# Revit family: Power-Fin Boiler PBN2500-5000_2014
name_source: partatom
category: Mechanical Equipment
revit_build: Autodesk Revit 2014 (Build: 20130308_1515(x64)
units: mm (PartAtom-declared; Revit-internal decimal feet)

## types (5) — shared parameters
# of Connections = 1
Control Voltage = 24
Description = Power-Fin Boiler
Drain Radius = 3/8"
Front Clearance Depth = 24"
Manufacturer = Lochinvar
SES BIM Studio # = 2016 0649 05
Top Clearance Depth = 24"
URL = http://www.lochinvar.com
WATER CONN SIZE = 4"
Water Conn Radius = 2"

## per-type parameters (varying)
- PBN2500: AIR INLET SIZE=9"; A_HEIGHT=59"; Air Inlet Radius=4 1/2"; B_LENGTH=44 1/2"; Back Clearance Length=36"; C_WIDTH=29 3/4"; D_Gas Conn Height=49 3/4"; Display Panel Height=6 1/2"; Display Panel width=10 3/4"; E_Gas Conn Offset From Left=4"; F_Vent Offset From Left=15"; GALLON CAPACITY=10.4; GAS CONN SIZE=2"; G_Vent Length=16"; Gas Conn Radius=1"; H_Air Inlet Offset From Top=9"; INPUT RATE (BTUH)=2500000; J_Air Inlet Offset from Left=20 1/4"; K_Water Inlet & Outlet Height=37"; L_Water Outlet Offset From Left=8 3/4"; M_Vent Height=23"; N_Water Inlet Offset From Left=21 1/4"; OUTPUT RATE (BTUH)=2175000; P_Pipe Length=12"; Q_Panel Height=40"; Total Amps=4.9; VENT SIZE=9"; Vent Radius=4 1/2"; Voltage/Heater=240V-1PH
- PBN3000: AIR INLET SIZE=9"; A_HEIGHT=65"; Air Inlet Radius=4 1/2"; B_LENGTH=44 1/2"; Back Clearance Length=36"; C_WIDTH=29 3/4"; D_Gas Conn Height=55 3/4"; Display Panel Height=7"; Display Panel width=10 3/4"; E_Gas Conn Offset From Left=4"; F_Vent Offset From Left=15"; GALLON CAPACITY=11.3; GAS CONN SIZE=2"; G_Vent Length=16 1/4"; Gas Conn Radius=1"; H_Air Inlet Offset From Top=9"; INPUT RATE (BTUH)=3000000; J_Air Inlet Offset from Left=20 1/4"; K_Water Inlet & Outlet Height=43"; L_Water Outlet Offset From Left=8 3/4"; M_Vent Height=23"; N_Water Inlet Offset From Left=21 1/4"; OUTPUT RATE (BTUH)=2610000; P_Pipe Length=12"; Q_Panel Height=45"; Total Amps=4.9; VENT SIZE=10"; Vent Radius=5"; Voltage/Heater=240V-1PH
- PBN3500: AIR INLET SIZE=10"; A_HEIGHT=70 1/4"; Air Inlet Radius=5"; B_LENGTH=47 1/4"; Back Clearance Length=36"; C_WIDTH=29 3/4"; D_Gas Conn Height=62 1/2"; Display Panel Height=6 1/8"; Display Panel width=10 1/2"; E_Gas Conn Offset From Left=8 1/4"; F_Vent Offset From Left=15"; GALLON CAPACITY=12.2; GAS CONN SIZE=2"; G_Vent Length=16 1/4"; Gas Conn Radius=1"; H_Air Inlet Offset From Top=9"; INPUT RATE (BTUH)=3500000; J_Air Inlet Offset from Left=20 1/4"; K_Water Inlet & Outlet Height=48 1/2"; L_Water Outlet Offset From Left=9"; M_Vent Height=23"; N_Water Inlet Offset From Left=21 1/2"; OUTPUT RATE (BTUH)=3045000; P_Pipe Length=12"; Q_Panel Height=52"; Total Amps=6.0; VENT SIZE=10"; Vent Radius=5"; Voltage/Heater=240V-3PH
- PBN4000: AIR INLET SIZE=10"; A_HEIGHT=79 3/4"; Air Inlet Radius=5"; B_LENGTH=47 1/4"; Back Clearance Length=36"; C_WIDTH=29 3/4"; D_Gas Conn Height=68 3/4"; Display Panel Height=7 5/8"; Display Panel width=10 1/2"; E_Gas Conn Offset From Left=8 1/4"; F_Vent Offset From Left=15"; GALLON CAPACITY=13.2; GAS CONN SIZE=2 1/2"; G_Vent Length=16 1/4"; Gas Conn Radius=1 1/4"; H_Air Inlet Offset From Top=10 1/2"; INPUT RATE (BTUH)=4000000; J_Air Inlet Offset from Left=20"; K_Water Inlet & Outlet Height=54"; L_Water Outlet Offset From Left=8 3/4"; M_Vent Height=22 1/4"; N_Water Inlet Offset From Left=21 1/4"; OUTPUT RATE (BTUH)=3840000; P_Pipe Length=12"; Q_Panel Height=58 1/2"; Total Amps=6.0; VENT SIZE=12"; Vent Radius=6"; Voltage/Heater=208V-3PH
- PBN5000: AIR INLET SIZE=12"; A_HEIGHT=93 1/4"; Air Inlet Radius=6"; B_LENGTH=46 3/4"; Back Clearance Length=37 1/4"; C_WIDTH=32 3/4"; D_Gas Conn Height=82 1/4"; Display Panel Height=8 7/8"; Display Panel width=12"; E_Gas Conn Offset From Left=10"; F_Vent Offset From Left=17"; GALLON CAPACITY=15; GAS CONN SIZE=2 1/2"; G_Vent Length=17 1/2"; Gas Conn Radius=1 1/4"; H_Air Inlet Offset From Top=11"; INPUT RATE (BTUH)=5000000; J_Air Inlet Offset from Left=23 1/2"; K_Water Inlet & Outlet Height=65 1/2"; L_Water Outlet Offset From Left=11 1/2"; M_Vent Height=22"; N_Water Inlet Offset From Left=24"; OUTPUT RATE (BTUH)=4350000; P_Pipe Length=13 1/4"; Q_Panel Height=69 1/2"; Total Amps=3.4; VENT SIZE=14"; Vent Radius=7"; Voltage/Heater=480V-3PH

note: column(s) folded — value = type name in every type: MODEL NO., Model

## geometry (parser evidence)
native form markers: Sweep x1
no freeform markers — native parametric forms only
